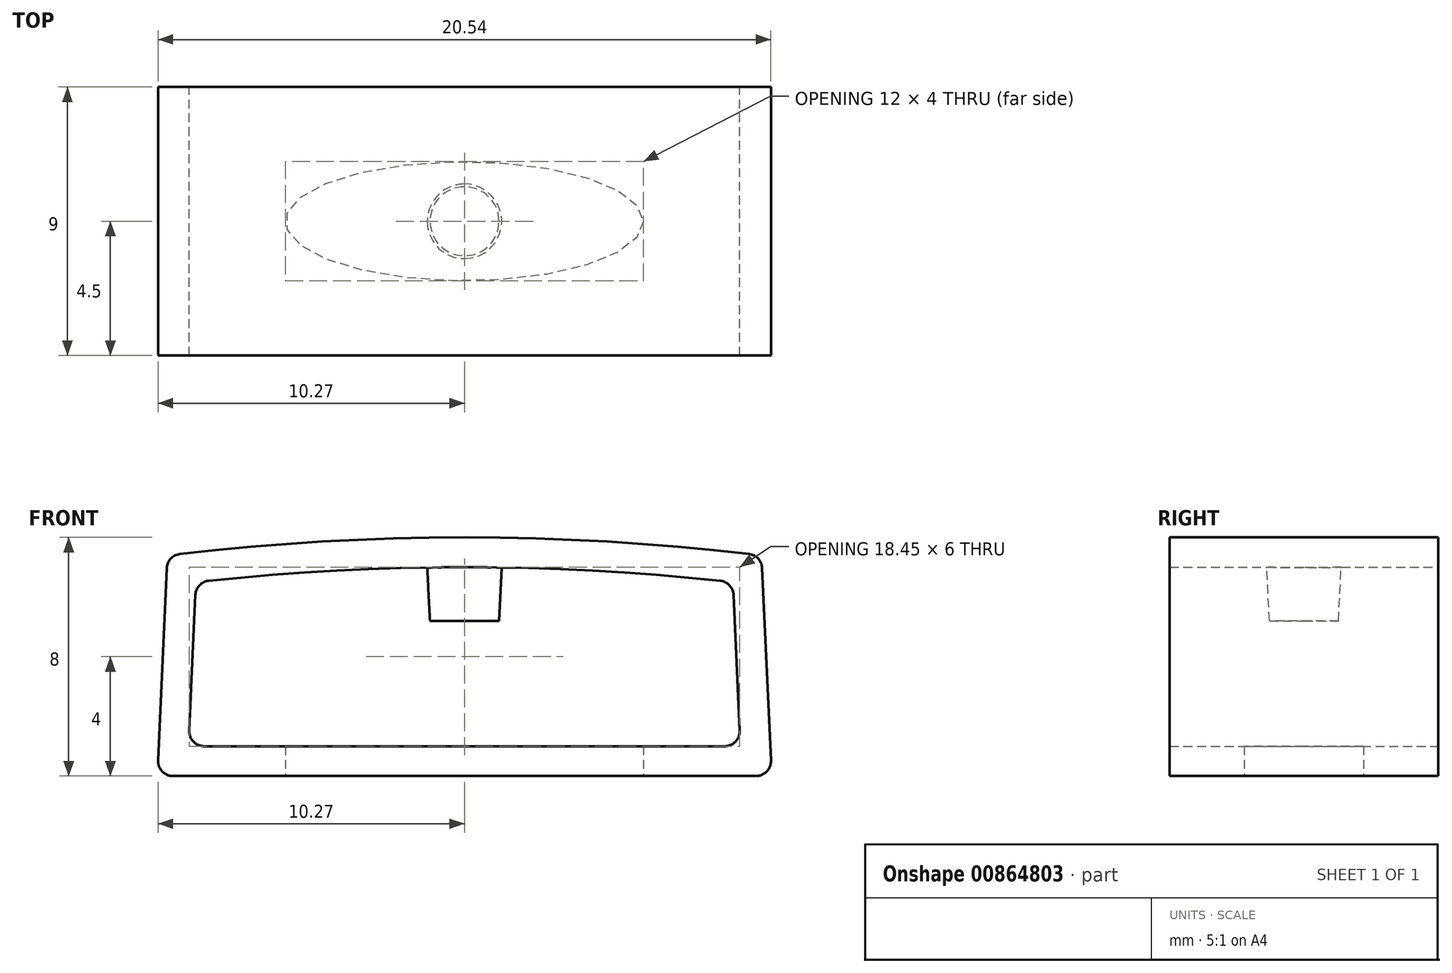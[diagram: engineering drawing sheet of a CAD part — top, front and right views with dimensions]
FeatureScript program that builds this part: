
annotation { "Feature Type Name" : "Feature", "Feature Type Description" : "" }
export const myFeature = defineFeature(function(context is Context, id is Id, definition is map)
    precondition{}
    {
        {
            var Q0;
            Q0=qCreatedBy(makeId("Front.planeOp"),FACE);
            var sketch = newSketch(context, id + "F0", { "sketchPlane" : qUnion([Q0])});
            skPoint(sketch, "E0.middle", {"position": v(0, 0) * mm});
            skLineSegment(sketch, "E1", {"start": v(0.02, 0.52) * mm, "end": v(0.23, 5.07) * mm});
            skLineSegment(sketch, "E2", {"start": v(0.25, 5.5) * mm, "end": v(18.25, 5.5) * mm, "construction": true});
            skLineSegment(sketch, "E3", {"start": v(18.27, 5.07) * mm, "end": v(18.48, 0.52) * mm});
            skLineSegment(sketch, "E4", {"start": v(17.98, 0) * mm, "end": v(0.52, 0) * mm});
            skArc(sketch, "E5", {"start": v(17.82, 5.55) * mm, "mid": v(9.25, 6) * mm, "end": v(0.68, 5.55) * mm});
            skArc(sketch, "E6.0", {"start": v(18.79, 6.45) * mm, "mid": v(9.25, 7) * mm, "end": v(-0.29, 6.45) * mm});
            skLineSegment(sketch, "E6.1", {"start": v(19.23, 5.97) * mm, "end": v(19.52, -0.48) * mm});
            skLineSegment(sketch, "E6.2", {"start": v(19.02, -1) * mm, "end": v(-0.52, -1) * mm});
            skLineSegment(sketch, "E6.3", {"start": v(-1.02, -0.48) * mm, "end": v(-0.73, 5.97) * mm});
            skPoint(sketch, "E7.visualSharp", {"position": v(0.25, 5.5) * mm});
            skArc(sketch, "E7.filletArc", {"start": v(0.68, 5.55) * mm, "mid": v(0.37, 5.4) * mm, "end": v(0.23, 5.07) * mm});
            skPoint(sketch, "E8.visualSharp", {"position": v(18.25, 5.5) * mm});
            skArc(sketch, "E8.filletArc", {"start": v(18.27, 5.07) * mm, "mid": v(18.13, 5.4) * mm, "end": v(17.82, 5.55) * mm});
            skPoint(sketch, "E9.visualSharp", {"position": v(18.5, 0) * mm});
            skArc(sketch, "E9.filletArc", {"start": v(17.98, 0) * mm, "mid": v(18.34, 0.15) * mm, "end": v(18.48, 0.52) * mm});
            skArc(sketch, "E10.filletArc", {"start": v(0.02, 0.52) * mm, "mid": v(0.16, 0.15) * mm, "end": v(0.52, 0) * mm});
            skPoint(sketch, "E11.visualSharp", {"position": v(-1.05, -1) * mm});
            skArc(sketch, "E11.filletArc", {"start": v(-1.02, -0.48) * mm, "mid": v(-0.88, -0.85) * mm, "end": v(-0.52, -1) * mm});
            skPoint(sketch, "E12.visualSharp", {"position": v(-0.71, 6.4) * mm});
            skArc(sketch, "E12.filletArc", {"start": v(-0.29, 6.45) * mm, "mid": v(-0.6, 6.29) * mm, "end": v(-0.73, 5.97) * mm});
            skPoint(sketch, "E13.visualSharp", {"position": v(19.21, 6.4) * mm});
            skArc(sketch, "E13.filletArc", {"start": v(19.23, 5.97) * mm, "mid": v(19.1, 6.29) * mm, "end": v(18.79, 6.45) * mm});
            skPoint(sketch, "E14.visualSharp", {"position": v(19.55, -1) * mm});
            skArc(sketch, "E14.filletArc", {"start": v(19.02, -1) * mm, "mid": v(19.38, -0.85) * mm, "end": v(19.52, -0.48) * mm});
            skSolve(sketch);
        }
        {
            var Q0;
            Q0 = qSketchRegion(id + "F0", true);
            extrude(context, id + "F1", {"entities" : qUnion([Q0]), "depth" : 9 * mm, "offsetDistance" : 25 * mm});
        }
        {
            var Q0;
            Q0=makeQuery(id+"F1.opExtrude","SWEPT_FACE",FACE,{"disambiguationData":[OSD([sQuery(id+"F0.wireOp",EDGE,"E6.2")])]});
            var sketch = newSketch(context, id + "F2", { "sketchPlane" : qUnion([Q0])});
            skEllipse(sketch, "E15", {"center": v(9.25, 4.5) * mm, "majorRadius": 6 * mm, "minorRadius": 2 * mm, "majorAxis": v(1, 0)});
            skPoint(sketch, "E15.centerSnap0", {"position": v(9.25, 0) * mm});
            skPoint(sketch, "E15.centerSnap1", {"position": v(-0.52, 4.5) * mm});
            skSolve(sketch);
        }
        {
            var Q0;
            Q0 = qSketchRegion(id + "F2", true);
            extrude(context, id + "F3", {"entities" : qUnion([Q0]), "operationType" : NewBodyOperationType.REMOVE, "endBound" : BoundingType.UP_TO_NEXT, "oppositeDirection" : true, "depth" : 25 * mm, "offsetDistance" : 25 * mm});
        }
        {
            var Q0;
            Q0=makeQuery(id+"F1.opExtrude","SWEPT_FACE",FACE,{"disambiguationData":[OSD([sQuery(id+"F0.wireOp",EDGE,"E6.2")])]});
            cPlane(context, id + "F4", {"entities" : qUnion([Q0]), "cplaneType" : CPlaneType.OFFSET, "offset" : 7 * mm, "oppositeDirection" : true, "width" : 150 * mm, "height" : 150 * mm});
        }
        {
            var Q0;
            Q0=qCreatedBy(id+"F4.planeOp",FACE);
            var sketch = newSketch(context, id + "F5", { "sketchPlane" : qUnion([Q0])});
            skLineSegment(sketch, "E16", {"start": v(-0.52, 4.5) * mm, "end": v(9.25, 4.5) * mm, "construction": true});
            skLineSegment(sketch, "E17", {"start": v(9.25, 4.5) * mm, "end": v(9.25, 0) * mm, "construction": true});
            skCircle(sketch, "E18", {"center": v(9.25, 4.5) * mm, "radius": 1.25 * mm});
            skSolve(sketch);
        }
        {
            var Q0;
            Q0 = qSketchRegion(id + "F5", true);
            extrude(context, id + "F6", {"entities" : qUnion([Q0]), "operationType" : NewBodyOperationType.ADD, "depth" : 1.8 * mm, "offsetDistance" : 25 * mm, "hasDraft" : true, "draftAngle" : 3 * degree, "draftPullDirection" : true});
        }
    });
